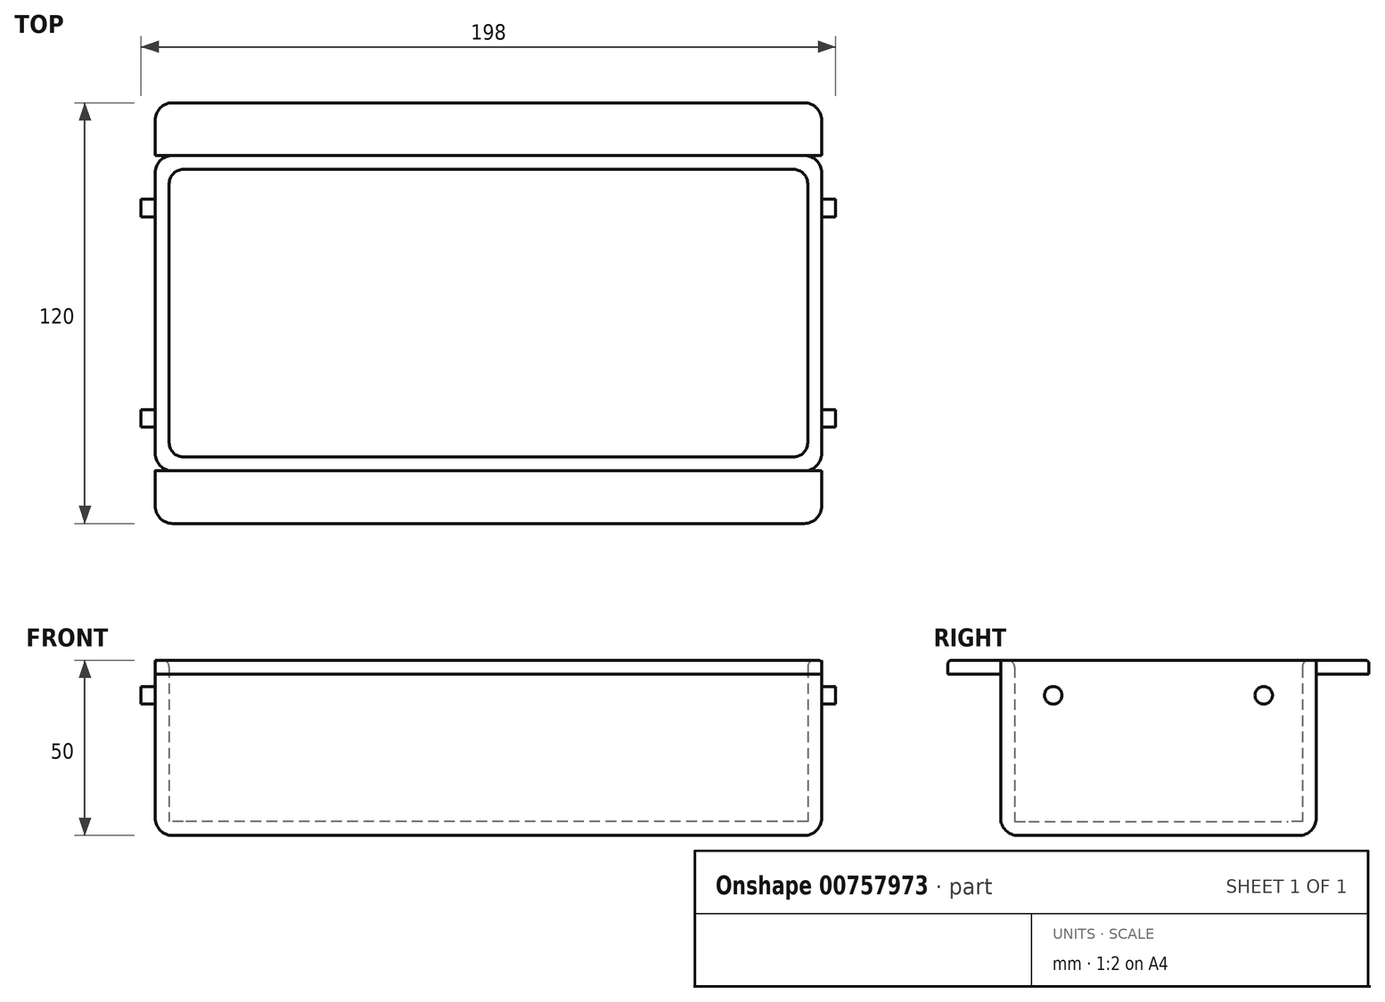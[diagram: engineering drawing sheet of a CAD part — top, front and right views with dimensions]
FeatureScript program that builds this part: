
annotation { "Feature Type Name" : "Feature", "Feature Type Description" : "" }
export const myFeature = defineFeature(function(context is Context, id is Id, definition is map)
    precondition{}
    {
        {
            var Q0;
            Q0=qCreatedBy(makeId("Top.planeOp"),FACE);
            var sketch = newSketch(context, id + "F0", { "sketchPlane" : qUnion([Q0])});
            skLineSegment(sketch, "E0.bottom", {"start": v(95, -45) * mm, "end": v(-95, -45) * mm});
            skLineSegment(sketch, "E0.top", {"start": v(95, 45) * mm, "end": v(-95, 45) * mm});
            skLineSegment(sketch, "E0.left", {"start": v(95, -45) * mm, "end": v(95, 45) * mm});
            skLineSegment(sketch, "E0.right", {"start": v(-95, -45) * mm, "end": v(-95, 45) * mm});
            skPoint(sketch, "E0.middle", {"position": v(0, 0) * mm});
            skLineSegment(sketch, "E1.0", {"start": v(91, 41) * mm, "end": v(-91, 41) * mm});
            skLineSegment(sketch, "E1.1", {"start": v(91, -41) * mm, "end": v(91, 41) * mm});
            skLineSegment(sketch, "E1.2", {"start": v(91, -41) * mm, "end": v(-91, -41) * mm});
            skLineSegment(sketch, "E1.3", {"start": v(-91, -41) * mm, "end": v(-91, 41) * mm});
            skSolve(sketch);
        }
        {
            var Q0;
            Q0=makeQuery(id+"F0.imprint","IMPRINT",FACE,{"disambiguationData":[TD([[makeQuery(id+"F0.imprint","IMPRINT",EDGE,{"derivedFrom":sQuery(id+"F0.wireOp",EDGE,"E0.bottom")}),-1.0]])]});
            extrude(context, id + "F1", {"entities" : qUnion([Q0]), "depth" : 46 * mm, "offsetDistance" : 25 * mm});
        }
        {
            var Q0;
            Q0=makeQuery(id+"F1.opExtrude","CAP_FACE",FACE,{"disambiguationData":[OSD([sQuery(id+"F0.wireOp",EDGE,"E0.bottom"),sQuery(id+"F0.wireOp",EDGE,"E0.top"),sQuery(id+"F0.wireOp",EDGE,"E0.left"),sQuery(id+"F0.wireOp",EDGE,"E0.right"),sQuery(id+"F0.wireOp",EDGE,"E1.0"),sQuery(id+"F0.wireOp",EDGE,"E1.1"),sQuery(id+"F0.wireOp",EDGE,"E1.2"),sQuery(id+"F0.wireOp",EDGE,"E1.3")])],"isStart":true});
            var sketch = newSketch(context, id + "F2", { "sketchPlane" : qUnion([Q0])});
            skLineSegment(sketch, "E2.bottom", {"start": v(-95, 45) * mm, "end": v(95, 45) * mm});
            skLineSegment(sketch, "E2.top", {"start": v(-95, -45) * mm, "end": v(95, -45) * mm});
            skLineSegment(sketch, "E2.left", {"start": v(-95, 45) * mm, "end": v(-95, -45) * mm});
            skLineSegment(sketch, "E2.right", {"start": v(95, 45) * mm, "end": v(95, -45) * mm});
            skSolve(sketch);
        }
        {
            var Q0;
            Q0=makeQuery(id+"F2.imprint","IMPRINT",FACE,{"disambiguationData":[TD([[makeQuery(id+"F2.imprint","IMPRINT",EDGE,{"derivedFrom":sQuery(id+"F2.wireOp",EDGE,"E2.bottom")}),1.0]])]});
            var Q1;
            Q1=makeQuery(id+"F2.imprint","IMPRINT",FACE,{"disambiguationData":[TD([[makeQuery(id+"F2.imprint","IMPRINT",EDGE,{"derivedFrom":makeQuery(id+"F1.opExtrude","CAP_EDGE",EDGE,{"disambiguationData":[OSD([sQuery(id+"F0.wireOp",EDGE,"E1.0")])],"isStart":true})}),-1.0]])]});
            extrude(context, id + "F3", {"entities" : qUnion([Q0, Q1]), "operationType" : NewBodyOperationType.ADD, "depth" : 4 * mm, "offsetDistance" : 25 * mm});
        }
        {
            var Q0;
            Q0=makeQuery(id+"F1.opExtrude","CAP_EDGE",EDGE,{"disambiguationData":[OSD([sQuery(id+"F0.wireOp",EDGE,"E1.0")])],"isStart":true});
            var Q1;
            Q1=makeQuery(id+"F1.opExtrude","CAP_EDGE",EDGE,{"disambiguationData":[OSD([sQuery(id+"F0.wireOp",EDGE,"E1.3")])],"isStart":true});
            var Q2;
            Q2=makeQuery(id+"F1.opExtrude","CAP_EDGE",EDGE,{"disambiguationData":[OSD([sQuery(id+"F0.wireOp",EDGE,"E1.1")])],"isStart":true});
            var Q3;
            Q3=makeQuery(id+"F1.opExtrude","CAP_EDGE",EDGE,{"disambiguationData":[OSD([sQuery(id+"F0.wireOp",EDGE,"E1.2")])],"isStart":true});
            var Q4;
            Q4=makeQuery(id+"F1.opExtrude","SWEPT_EDGE",EDGE,{"disambiguationData":[OSD([sQuery(id+"F0.wireOp",EDGE,"E1.1"),sQuery(id+"F0.wireOp",EDGE,"E1.2")])]});
            var Q5;
            Q5=makeQuery(id+"F1.opExtrude","SWEPT_EDGE",EDGE,{"disambiguationData":[OSD([sQuery(id+"F0.wireOp",EDGE,"E1.0"),sQuery(id+"F0.wireOp",EDGE,"E1.1")])]});
            var Q6;
            Q6=makeQuery(id+"F1.opExtrude","SWEPT_EDGE",EDGE,{"disambiguationData":[OSD([sQuery(id+"F0.wireOp",EDGE,"E1.0"),sQuery(id+"F0.wireOp",EDGE,"E1.3")])]});
            var Q7;
            Q7=makeQuery(id+"F1.opExtrude","SWEPT_EDGE",EDGE,{"disambiguationData":[OSD([sQuery(id+"F0.wireOp",EDGE,"E1.2"),sQuery(id+"F0.wireOp",EDGE,"E1.3")])]});
            fillet(context, id + "F4", {"entities" : qUnion([Q0, Q1, Q2, Q3, Q4, Q5, Q6, Q7]), "radius" : 4 * mm, "tangentPropagation" : true, "allowEdgeOverflow" : false});
        }
        {
            var Q0;
            Q0=makeQuery(id+"F1.opExtrude","CAP_FACE",FACE,{"disambiguationData":[OSD([sQuery(id+"F0.wireOp",EDGE,"E0.bottom"),sQuery(id+"F0.wireOp",EDGE,"E0.top"),sQuery(id+"F0.wireOp",EDGE,"E0.left"),sQuery(id+"F0.wireOp",EDGE,"E0.right"),sQuery(id+"F0.wireOp",EDGE,"E1.0"),sQuery(id+"F0.wireOp",EDGE,"E1.1"),sQuery(id+"F0.wireOp",EDGE,"E1.2"),sQuery(id+"F0.wireOp",EDGE,"E1.3")])],"isStart":false});
            var sketch = newSketch(context, id + "F5", { "sketchPlane" : qUnion([Q0])});
            skLineSegment(sketch, "E3.bottom", {"start": v(-95, 45) * mm, "end": v(95, 45) * mm});
            skLineSegment(sketch, "E3.top", {"start": v(-95, -45) * mm, "end": v(95, -45) * mm});
            skLineSegment(sketch, "E3.left", {"start": v(-95, 45) * mm, "end": v(-95, -45) * mm});
            skLineSegment(sketch, "E3.right", {"start": v(95, 45) * mm, "end": v(95, -45) * mm});
            skLineSegment(sketch, "E4.0", {"start": v(-95, 60) * mm, "end": v(95, 60) * mm});
            skLineSegment(sketch, "E5.0", {"start": v(-95, -60) * mm, "end": v(95, -60) * mm});
            skLineSegment(sketch, "E6", {"start": v(-95, 45) * mm, "end": v(-95, 60) * mm});
            skLineSegment(sketch, "E7", {"start": v(-95, -60) * mm, "end": v(-95, -45) * mm});
            skLineSegment(sketch, "E8", {"start": v(95, -60) * mm, "end": v(95, -45) * mm});
            skLineSegment(sketch, "E9", {"start": v(95, 45) * mm, "end": v(95, 60) * mm});
            skSolve(sketch);
        }
        {
            var Q0;
            Q0=makeQuery(id+"F5.imprint","IMPRINT",FACE,{"disambiguationData":[TD([[makeQuery(id+"F5.imprint","IMPRINT",EDGE,{"derivedFrom":sQuery(id+"F5.wireOp",EDGE,"E3.top")}),1.0]])]});
            var Q1;
            Q1=makeQuery(id+"F5.imprint","IMPRINT",FACE,{"disambiguationData":[TD([[makeQuery(id+"F5.imprint","IMPRINT",EDGE,{"derivedFrom":sQuery(id+"F5.wireOp",EDGE,"E3.bottom")}),-1.0]])]});
            extrude(context, id + "F6", {"entities" : qUnion([Q0, Q1]), "oppositeDirection" : true, "depth" : 4 * mm, "offsetDistance" : 25 * mm});
        }
        {
            var Q0;
            Q0=makeQuery(id+"F6.opExtrude","SWEPT_EDGE",EDGE,{"disambiguationData":[OSD([sQuery(id+"F5.wireOp",EDGE,"E5.0"),sQuery(id+"F5.wireOp",EDGE,"E7")])]});
            var Q1;
            Q1=makeQuery(id+"F6.opExtrude","SWEPT_EDGE",EDGE,{"disambiguationData":[OSD([sQuery(id+"F5.wireOp",EDGE,"E5.0"),sQuery(id+"F5.wireOp",EDGE,"E8")])]});
            var Q2;
            Q2=makeQuery(id+"F6.opExtrude","SWEPT_EDGE",EDGE,{"disambiguationData":[OSD([sQuery(id+"F5.wireOp",EDGE,"E4.0"),sQuery(id+"F5.wireOp",EDGE,"E9")])]});
            var Q3;
            Q3=makeQuery(id+"F6.opExtrude","SWEPT_EDGE",EDGE,{"disambiguationData":[OSD([sQuery(id+"F5.wireOp",EDGE,"E4.0"),sQuery(id+"F5.wireOp",EDGE,"E6")])]});
            fillet(context, id + "F7", {"entities" : qUnion([Q0, Q1, Q2, Q3]), "radius" : 5 * mm, "tangentPropagation" : true, "allowEdgeOverflow" : false});
        }
        {
            var Q0;
            Q0=makeQuery(id+"F1.opExtrude","CAP_EDGE",EDGE,{"disambiguationData":[OSD([sQuery(id+"F0.wireOp",EDGE,"E1.0")])],"isStart":false});
            var Q1;
            {var subQ0=sQuery(id+"F0.wireOp",EDGE,"E1.1");var subQ1=sQuery(id+"F0.wireOp",EDGE,"E1.0");Q1=makeQuery(id+"F4.opFillet","BLEND_EDGE",EDGE,{"blendedFrom":[makeQuery(id+"F1.opExtrude","SWEPT_EDGE",EDGE,{"disambiguationData":[OSD([subQ1,subQ0])]}),makeQuery(id+"F1.opExtrude","CAP_FACE",FACE,{"disambiguationData":[OSD([sQuery(id+"F0.wireOp",EDGE,"E0.bottom"),sQuery(id+"F0.wireOp",EDGE,"E0.top"),sQuery(id+"F0.wireOp",EDGE,"E0.left"),sQuery(id+"F0.wireOp",EDGE,"E0.right"),subQ1,subQ0,sQuery(id+"F0.wireOp",EDGE,"E1.2"),sQuery(id+"F0.wireOp",EDGE,"E1.3")])],"isStart":false})],"blendedInto":[makeQuery(id+"F1.opExtrude","CAP_FACE",FACE,{"disambiguationData":[OSD([sQuery(id+"F0.wireOp",EDGE,"E0.bottom"),sQuery(id+"F0.wireOp",EDGE,"E0.top"),sQuery(id+"F0.wireOp",EDGE,"E0.left"),sQuery(id+"F0.wireOp",EDGE,"E0.right"),subQ1,subQ0,sQuery(id+"F0.wireOp",EDGE,"E1.2"),sQuery(id+"F0.wireOp",EDGE,"E1.3")])],"isStart":false})]});}
            fillet(context, id + "F8", {"entities" : qUnion([Q0, Q1]), "radius" : 2 * mm, "tangentPropagation" : true, "allowEdgeOverflow" : false});
        }
        {
            var Q0;
            Q0=makeQuery(id+"F6.opExtrude","CAP_EDGE",EDGE,{"disambiguationData":[OSD([sQuery(id+"F5.wireOp",EDGE,"E6")])],"isStart":true});
            var Q1;
            Q1=makeQuery(id+"F6.opExtrude","CAP_EDGE",EDGE,{"disambiguationData":[OSD([sQuery(id+"F5.wireOp",EDGE,"E7")])],"isStart":true});
            fillet(context, id + "F9", {"entities" : qUnion([Q0, Q1]), "radius" : 1 * mm, "tangentPropagation" : true, "allowEdgeOverflow" : false});
        }
        {
            var Q0;
            Q0=makeQuery(id+"F3.boolean.opBoolean","MERGE",EDGE,{"derivedFrom":[makeQuery(id+"F1.opExtrude","SWEPT_EDGE",EDGE,{"disambiguationData":[OSD([sQuery(id+"F0.wireOp",EDGE,"E0.top"),sQuery(id+"F0.wireOp",EDGE,"E0.left")])]}),makeQuery(id+"F3.opExtrude","SWEPT_EDGE",EDGE,{"disambiguationData":[OSD([sQuery(id+"F2.wireOp",EDGE,"E2.top"),sQuery(id+"F2.wireOp",EDGE,"E2.right")])]})]});
            var Q1;
            Q1=makeQuery(id+"F3.opExtrude","CAP_EDGE",EDGE,{"disambiguationData":[OSD([sQuery(id+"F2.wireOp",EDGE,"E2.top")])],"isStart":false});
            var Q2;
            Q2=makeQuery(id+"F3.boolean.opBoolean","MERGE",EDGE,{"derivedFrom":[makeQuery(id+"F1.opExtrude","SWEPT_EDGE",EDGE,{"disambiguationData":[OSD([sQuery(id+"F0.wireOp",EDGE,"E0.top"),sQuery(id+"F0.wireOp",EDGE,"E0.right")])]}),makeQuery(id+"F3.opExtrude","SWEPT_EDGE",EDGE,{"disambiguationData":[OSD([sQuery(id+"F2.wireOp",EDGE,"E2.top"),sQuery(id+"F2.wireOp",EDGE,"E2.left")])]})]});
            var Q3;
            Q3=makeQuery(id+"F3.opExtrude","CAP_EDGE",EDGE,{"disambiguationData":[OSD([sQuery(id+"F2.wireOp",EDGE,"E2.left")])],"isStart":false});
            var Q4;
            Q4=makeQuery(id+"F3.opExtrude","CAP_EDGE",EDGE,{"disambiguationData":[OSD([sQuery(id+"F2.wireOp",EDGE,"E2.bottom")])],"isStart":false});
            var Q5;
            Q5=makeQuery(id+"F3.opExtrude","CAP_EDGE",EDGE,{"disambiguationData":[OSD([sQuery(id+"F2.wireOp",EDGE,"E2.right")])],"isStart":false});
            var Q6;
            Q6=makeQuery(id+"F3.boolean.opBoolean","MERGE",EDGE,{"derivedFrom":[makeQuery(id+"F1.opExtrude","SWEPT_EDGE",EDGE,{"disambiguationData":[OSD([sQuery(id+"F0.wireOp",EDGE,"E0.bottom"),sQuery(id+"F0.wireOp",EDGE,"E0.left")])]}),makeQuery(id+"F3.opExtrude","SWEPT_EDGE",EDGE,{"disambiguationData":[OSD([sQuery(id+"F2.wireOp",EDGE,"E2.bottom"),sQuery(id+"F2.wireOp",EDGE,"E2.right")])]})]});
            var Q7;
            Q7=makeQuery(id+"F3.boolean.opBoolean","MERGE",EDGE,{"derivedFrom":[makeQuery(id+"F1.opExtrude","SWEPT_EDGE",EDGE,{"disambiguationData":[OSD([sQuery(id+"F0.wireOp",EDGE,"E0.bottom"),sQuery(id+"F0.wireOp",EDGE,"E0.right")])]}),makeQuery(id+"F3.opExtrude","SWEPT_EDGE",EDGE,{"disambiguationData":[OSD([sQuery(id+"F2.wireOp",EDGE,"E2.bottom"),sQuery(id+"F2.wireOp",EDGE,"E2.left")])]})]});
            fillet(context, id + "F10", {"entities" : qUnion([Q0, Q1, Q2, Q3, Q4, Q5, Q6, Q7]), "radius" : 5 * mm, "tangentPropagation" : true, "allowEdgeOverflow" : false});
        }
        {
            var Q0;
            Q0=makeQuery(id+"F3.boolean.opBoolean","MERGE",FACE,{"derivedFrom":[makeQuery(id+"F1.opExtrude","SWEPT_FACE",FACE,{"disambiguationData":[OSD([sQuery(id+"F0.wireOp",EDGE,"E0.right")])]}),makeQuery(id+"F3.opExtrude","SWEPT_FACE",FACE,{"disambiguationData":[OSD([sQuery(id+"F2.wireOp",EDGE,"E2.left")])]})]});
            var sketch = newSketch(context, id + "F11", { "sketchPlane" : qUnion([Q0])});
            skCircle(sketch, "E10", {"center": v(-30, 36) * mm, "radius": 2.5 * mm});
            skCircle(sketch, "E11", {"center": v(30, 36) * mm, "radius": 2.5 * mm});
            skSolve(sketch);
        }
        {
            var Q0;
            Q0=makeQuery(id+"F11.imprint","IMPRINT",FACE,{"disambiguationData":[TD([[makeQuery(id+"F11.imprint","IMPRINT",EDGE,{"derivedFrom":sQuery(id+"F11.wireOp",EDGE,"E10")}),1.0]])]});
            var Q1;
            Q1=makeQuery(id+"F11.imprint","IMPRINT",FACE,{"disambiguationData":[TD([[makeQuery(id+"F11.imprint","IMPRINT",EDGE,{"derivedFrom":sQuery(id+"F11.wireOp",EDGE,"E11")}),1.0]])]});
            extrude(context, id + "F12", {"entities" : qUnion([Q0, Q1]), "operationType" : NewBodyOperationType.ADD, "depth" : 4 * mm, "offsetDistance" : 25 * mm});
        }
        {
            var Q0;
            Q0=makeQuery(id+"F3.boolean.opBoolean","MERGE",FACE,{"derivedFrom":[makeQuery(id+"F1.opExtrude","SWEPT_FACE",FACE,{"disambiguationData":[OSD([sQuery(id+"F0.wireOp",EDGE,"E0.left")])]}),makeQuery(id+"F3.opExtrude","SWEPT_FACE",FACE,{"disambiguationData":[OSD([sQuery(id+"F2.wireOp",EDGE,"E2.right")])]})]});
            var sketch = newSketch(context, id + "F13", { "sketchPlane" : qUnion([Q0])});
            skCircle(sketch, "E12", {"center": v(-30, 36) * mm, "radius": 2.5 * mm});
            skCircle(sketch, "E13", {"center": v(30, 36) * mm, "radius": 2.5 * mm});
            skSolve(sketch);
        }
        {
            var Q0;
            Q0=makeQuery(id+"F13.imprint","IMPRINT",FACE,{"disambiguationData":[TD([[makeQuery(id+"F13.imprint","IMPRINT",EDGE,{"derivedFrom":sQuery(id+"F13.wireOp",EDGE,"E12")}),1.0]])]});
            var Q1;
            Q1=makeQuery(id+"F13.imprint","IMPRINT",FACE,{"disambiguationData":[TD([[makeQuery(id+"F13.imprint","IMPRINT",EDGE,{"derivedFrom":sQuery(id+"F13.wireOp",EDGE,"E13")}),1.0]])]});
            extrude(context, id + "F14", {"entities" : qUnion([Q0, Q1]), "operationType" : NewBodyOperationType.ADD, "depth" : 4 * mm, "offsetDistance" : 25 * mm});
        }
    });
